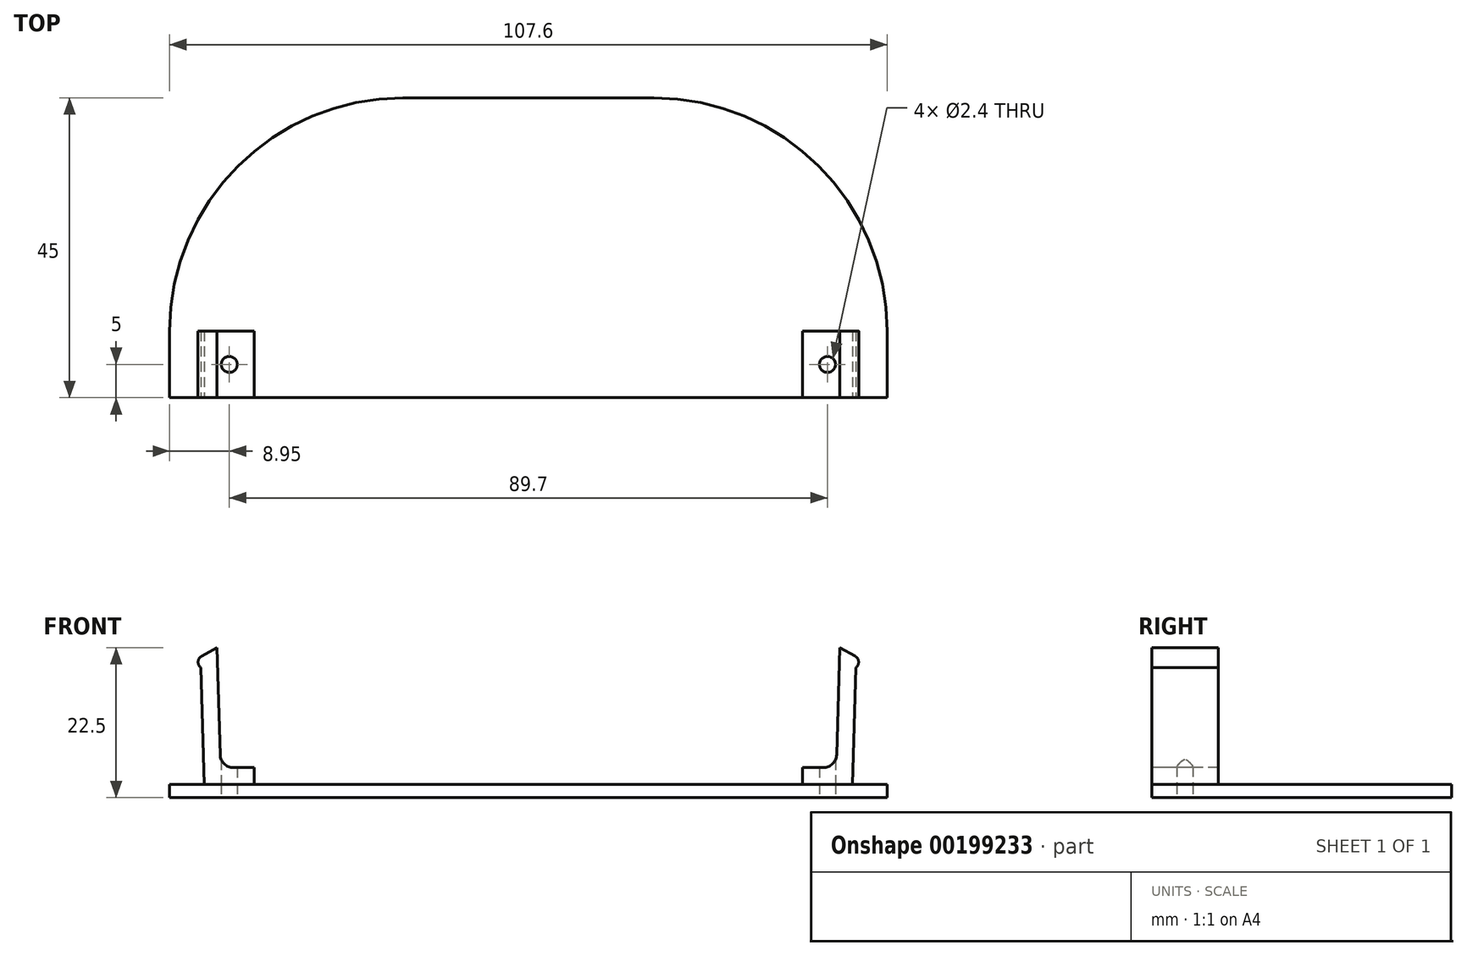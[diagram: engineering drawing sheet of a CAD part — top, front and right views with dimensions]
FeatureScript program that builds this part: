
annotation { "Feature Type Name" : "Feature", "Feature Type Description" : "" }
export const myFeature = defineFeature(function(context is Context, id is Id, definition is map)
    precondition{}
    {
        {
            var Q0;
            Q0=qCreatedBy(makeId("Top.planeOp"),FACE);
            var sketch = newSketch(context, id + "F0", { "sketchPlane" : qUnion([Q0])});
            skLineSegment(sketch, "E0", {"start": v(0, 0) * mm, "end": v(0, 40) * mm, "construction": true});
            skLineSegment(sketch, "E1.bottom", {"start": v(-18.8, 40) * mm, "end": v(18.8, 40) * mm});
            skLineSegment(sketch, "E1.left", {"start": v(-48.8, 10) * mm, "end": v(-48.8, 0) * mm});
            skLineSegment(sketch, "E1.right", {"start": v(48.8, 10) * mm, "end": v(48.8, 0) * mm});
            skLineSegment(sketch, "E2", {"start": v(-48.8, 0) * mm, "end": v(48.8, 0) * mm});
            skPoint(sketch, "E3.visualSharp", {"position": v(-48.8, 40) * mm});
            skArc(sketch, "E3.filletArc", {"start": v(-18.8, 40) * mm, "mid": v(-40.01, 31.21) * mm, "end": v(-48.8, 10) * mm});
            skPoint(sketch, "E4.visualSharp", {"position": v(48.8, 40) * mm});
            skArc(sketch, "E4.filletArc", {"start": v(48.8, 10) * mm, "mid": v(40.01, 31.21) * mm, "end": v(18.8, 40) * mm});
            skLineSegment(sketch, "E5.0", {"start": v(-53.8, 10) * mm, "end": v(-53.8, 0) * mm});
            skLineSegment(sketch, "E5.1", {"start": v(53.8, 10) * mm, "end": v(53.8, 0) * mm});
            skArc(sketch, "E5.2", {"start": v(53.8, 10) * mm, "mid": v(43.55, 34.75) * mm, "end": v(18.8, 45) * mm});
            skLineSegment(sketch, "E5.3", {"start": v(-18.8, 45) * mm, "end": v(18.8, 45) * mm});
            skArc(sketch, "E5.4", {"start": v(-18.8, 45) * mm, "mid": v(-43.55, 34.75) * mm, "end": v(-53.8, 10) * mm});
            skLineSegment(sketch, "E6", {"start": v(-53.8, 0) * mm, "end": v(-48.8, 0) * mm, "construction": true});
            skLineSegment(sketch, "E7", {"start": v(48.8, 0) * mm, "end": v(53.8, 0) * mm, "construction": true});
            skLineSegment(sketch, "E8", {"start": v(-53.8, 0) * mm, "end": v(-53.8, 0) * mm});
            skLineSegment(sketch, "E9", {"start": v(-53.8, 0) * mm, "end": v(-48.8, 0) * mm});
            skLineSegment(sketch, "E10", {"start": v(-48.8, 0) * mm, "end": v(-48.8, 0) * mm});
            skLineSegment(sketch, "E11", {"start": v(48.8, 0) * mm, "end": v(48.8, 0) * mm});
            skLineSegment(sketch, "E12", {"start": v(48.8, 0) * mm, "end": v(53.8, 0) * mm});
            skLineSegment(sketch, "E13", {"start": v(53.8, 0) * mm, "end": v(53.8, 0) * mm});
            skLineSegment(sketch, "E14", {"start": v(-53.8, 10) * mm, "end": v(-48.8, 10) * mm});
            skLineSegment(sketch, "E15", {"start": v(48.8, 10) * mm, "end": v(53.8, 10) * mm});
            skSolve(sketch);
        }
        {
            var Q0;
            Q0=makeQuery(id+"F0.imprint","IMPRINT",FACE,{"disambiguationData":[TD([[makeQuery(id+"F0.imprint","IMPRINT",EDGE,{"derivedFrom":sQuery(id+"F0.wireOp",EDGE,"E1.bottom")}),-1.0]])]});
            var Q1;
            Q1=makeQuery(id+"F0.imprint","IMPRINT",FACE,{"disambiguationData":[TD([[makeQuery(id+"F0.imprint","IMPRINT",EDGE,{"derivedFrom":sQuery(id+"F0.wireOp",EDGE,"E1.bottom")}),1.0]])]});
            var Q2;
            Q2=makeQuery(id+"F0.imprint","IMPRINT",FACE,{"disambiguationData":[TD([[makeQuery(id+"F0.imprint","IMPRINT",EDGE,{"derivedFrom":sQuery(id+"F0.wireOp",EDGE,"E1.right")}),1.0]])]});
            var Q3;
            Q3=makeQuery(id+"F0.imprint","IMPRINT",FACE,{"disambiguationData":[TD([[makeQuery(id+"F0.imprint","IMPRINT",EDGE,{"derivedFrom":sQuery(id+"F0.wireOp",EDGE,"E1.left")}),-1.0]])]});
            extrude(context, id + "F1", {"entities" : qUnion([Q0, Q1, Q2, Q3]), "depth" : 2 * mm});
        }
        {
            var Q0;
            Q0=makeQuery(id+"F1.opExtrude","SWEPT_FACE",FACE,{"disambiguationData":[OSD([sQuery(id+"F0.wireOp",EDGE,"E2"),sQuery(id+"F0.wireOp",EDGE,"E9"),sQuery(id+"F0.wireOp",EDGE,"E12")])]});
            var sketch = newSketch(context, id + "F2", { "sketchPlane" : qUnion([Q0])});
            skLineSegment(sketch, "E16", {"start": v(0, -14.06) * mm, "end": v(0, 16.95) * mm});
            skPoint(sketch, "E16.endSnap0", {"position": v(0, 2) * mm});
            skLineSegment(sketch, "E17", {"start": v(46.1, 2) * mm, "end": v(46.69, 22.5) * mm});
            skLineSegment(sketch, "E18", {"start": v(46.69, 22.5) * mm, "end": v(50.3, 20.5) * mm});
            skLineSegment(sketch, "E19", {"start": v(50.3, 20.5) * mm, "end": v(49.1, 19.5) * mm});
            skLineSegment(sketch, "E20", {"start": v(49.1, 19.5) * mm, "end": v(48.6, 2) * mm});
            skLineSegment(sketch, "E21.MirrorCS", {"start": v(-46.1, 2) * mm, "end": v(-46.69, 22.5) * mm});
            skLineSegment(sketch, "E22.MirrorCS", {"start": v(-46.69, 22.5) * mm, "end": v(-50.3, 20.5) * mm});
            skLineSegment(sketch, "E23.MirrorCS", {"start": v(-50.3, 20.5) * mm, "end": v(-49.1, 19.5) * mm});
            skLineSegment(sketch, "E24.MirrorCS", {"start": v(-49.1, 19.5) * mm, "end": v(-48.6, 2) * mm});
            skLineSegment(sketch, "E25", {"start": v(46.17, 4.5) * mm, "end": v(41.1, 4.5) * mm});
            skLineSegment(sketch, "E26", {"start": v(41.1, 4.5) * mm, "end": v(41.1, 2) * mm});
            skLineSegment(sketch, "E27", {"start": v(41.1, 2) * mm, "end": v(46.1, 2) * mm});
            skLineSegment(sketch, "E28.MirrorCS", {"start": v(-41.1, 4.5) * mm, "end": v(-41.1, 2) * mm});
            skLineSegment(sketch, "E29.MirrorCS", {"start": v(-46.17, 4.5) * mm, "end": v(-41.1, 4.5) * mm});
            skLineSegment(sketch, "E30.MirrorCS", {"start": v(-41.1, 2) * mm, "end": v(-46.1, 2) * mm});
            skSolve(sketch);
        }
        {
            var Q0;
            {var subQ0=sQuery(id+"F2.wireOp",EDGE,"E22.MirrorCS");Q0=makeQuery(id+"F2.imprint","IMPRINT",FACE,{"disambiguationData":[TD([[makeQuery(id+"F2.imprint","IMPRINT",EDGE,{"derivedFrom":subQ0}),1.0]])]});}
            var Q1;
            Q1=makeQuery(id+"F2.imprint","IMPRINT",FACE,{"disambiguationData":[TD([[makeQuery(id+"F2.imprint","IMPRINT",EDGE,{"derivedFrom":sQuery(id+"F2.wireOp",EDGE,"E28.MirrorCS")}),-1.0]])]});
            var Q2;
            {var subQ2=sQuery(id+"F2.wireOp",EDGE,"E25");Q2=makeQuery(id+"F2.imprint","IMPRINT",FACE,{"disambiguationData":[TD([[makeQuery(id+"F2.imprint","IMPRINT",EDGE,{"derivedFrom":subQ2}),1.0]])]});}
            var Q3;
            {var subQ0=sQuery(id+"F2.wireOp",EDGE,"E18");Q3=makeQuery(id+"F2.imprint","IMPRINT",FACE,{"disambiguationData":[TD([[makeQuery(id+"F2.imprint","IMPRINT",EDGE,{"derivedFrom":subQ0}),-1.0]])]});}
            extrude(context, id + "F3", {"entities" : qUnion([Q0, Q1, Q2, Q3]), "oppositeDirection" : true, "depth" : 10 * mm});
        }
        {
            var Q0;
            Q0=makeQuery(id+"F3.opExtrude","SWEPT_EDGE",EDGE,{"disambiguationData":[OSD([sQuery(id+"F2.wireOp",EDGE,"E17"),sQuery(id+"F2.wireOp",EDGE,"E25")])]});
            var Q1;
            Q1=makeQuery(id+"F3.opExtrude","SWEPT_EDGE",EDGE,{"disambiguationData":[OSD([sQuery(id+"F2.wireOp",EDGE,"E21.MirrorCS"),sQuery(id+"F2.wireOp",EDGE,"E29.MirrorCS")])]});
            fillet(context, id + "F4", {"entities" : qUnion([Q0, Q1]), "radius" : 2 * mm, "tangentPropagation" : true, "allowEdgeOverflow" : false});
        }
        {
            var Q0;
            Q0=makeQuery(id+"F3.opExtrude","SWEPT_EDGE",EDGE,{"disambiguationData":[OSD([sQuery(id+"F2.wireOp",EDGE,"E18"),sQuery(id+"F2.wireOp",EDGE,"E19")])]});
            var Q1;
            Q1=makeQuery(id+"F3.opExtrude","SWEPT_EDGE",EDGE,{"disambiguationData":[OSD([sQuery(id+"F2.wireOp",EDGE,"E22.MirrorCS"),sQuery(id+"F2.wireOp",EDGE,"E23.MirrorCS")])]});
            fillet(context, id + "F5", {"entities" : qUnion([Q0, Q1]), "radius" : 1 * mm, "tangentPropagation" : true, "allowEdgeOverflow" : false});
        }
        {
            var Q0;
            Q0=makeQuery(id+"F0.imprint","IMPRINT",FACE,{"disambiguationData":[TD([[makeQuery(id+"F0.imprint","IMPRINT",EDGE,{"derivedFrom":sQuery(id+"F0.wireOp",EDGE,"E1.bottom")}),-1.0]])]});
            var sketch = newSketch(context, id + "F6", { "sketchPlane" : qUnion([Q0])});
            skPoint(sketch, "E31", {"position": v(44.85, 5) * mm});
            skPoint(sketch, "E32", {"position": v(-44.85, 5) * mm});
            skSolve(sketch);
        }
        {
            var Q0;
            Q0=sQuery(id+"F6.wireOp",VERTEX,"E31");
            var Q1;
            Q1=sQuery(id+"F6.wireOp",VERTEX,"E32");
            var Q2;
            Q2=makeQuery(id+"F1.opExtrude","SWEPT_BODY",BODY,{"disambiguationData":[OSD([sQuery(id+"F0.wireOp",EDGE,"E2"),sQuery(id+"F0.wireOp",EDGE,"E5.0"),sQuery(id+"F0.wireOp",EDGE,"E5.1"),sQuery(id+"F0.wireOp",EDGE,"E5.2"),sQuery(id+"F0.wireOp",EDGE,"E5.3"),sQuery(id+"F0.wireOp",EDGE,"E5.4"),sQuery(id+"F0.wireOp",EDGE,"E9"),sQuery(id+"F0.wireOp",EDGE,"E12")])]});
            var Q3;
            Q3=makeQuery(id+"F3.opExtrude","SWEPT_BODY",BODY,{"disambiguationData":[OSD([sQuery(id+"F0.wireOp",EDGE,"E2"),sQuery(id+"F0.wireOp",EDGE,"E9"),sQuery(id+"F0.wireOp",EDGE,"E12"),sQuery(id+"F2.wireOp",EDGE,"E17"),sQuery(id+"F2.wireOp",EDGE,"E18"),sQuery(id+"F2.wireOp",EDGE,"E19"),sQuery(id+"F2.wireOp",EDGE,"E20"),sQuery(id+"F2.wireOp",EDGE,"E25"),sQuery(id+"F2.wireOp",EDGE,"E26"),sQuery(id+"F2.wireOp",EDGE,"E27")])]});
            var Q4;
            Q4=makeQuery(id+"F3.opExtrude","SWEPT_BODY",BODY,{"disambiguationData":[OSD([sQuery(id+"F0.wireOp",EDGE,"E2"),sQuery(id+"F0.wireOp",EDGE,"E9"),sQuery(id+"F0.wireOp",EDGE,"E12"),sQuery(id+"F2.wireOp",EDGE,"E21.MirrorCS"),sQuery(id+"F2.wireOp",EDGE,"E22.MirrorCS"),sQuery(id+"F2.wireOp",EDGE,"E23.MirrorCS"),sQuery(id+"F2.wireOp",EDGE,"E24.MirrorCS"),sQuery(id+"F2.wireOp",EDGE,"E28.MirrorCS"),sQuery(id+"F2.wireOp",EDGE,"E29.MirrorCS"),sQuery(id+"F2.wireOp",EDGE,"E30.MirrorCS")])]});
            hole(context, id + "F7", {"style" : HoleStyle.SIMPLE, "endStyle" : HoleEndStyle.BLIND, "oppositeDirection" : true, "standardTappedOrClearance" : lookupTablePath({ "standard" : "ISO", "engagement" : "75%", "pitch" : "0.6 mm", "size" : "M3", "type" : "Tapped" }), "standardBlindInLast" : lookupTablePath({ "standard" : "ISO", "engagement" : "75%", "pitch" : "0.6 mm", "size" : "M3", "type" : "Tapped" }), "holeDiameter" : 2.4 * mm, "holeDepth" : 6 * mm, "startFromSketch" : true, "locations" : qUnion([Q0, Q1]), "scope" : qUnion([Q2, Q3, Q4])});
        }
    });
